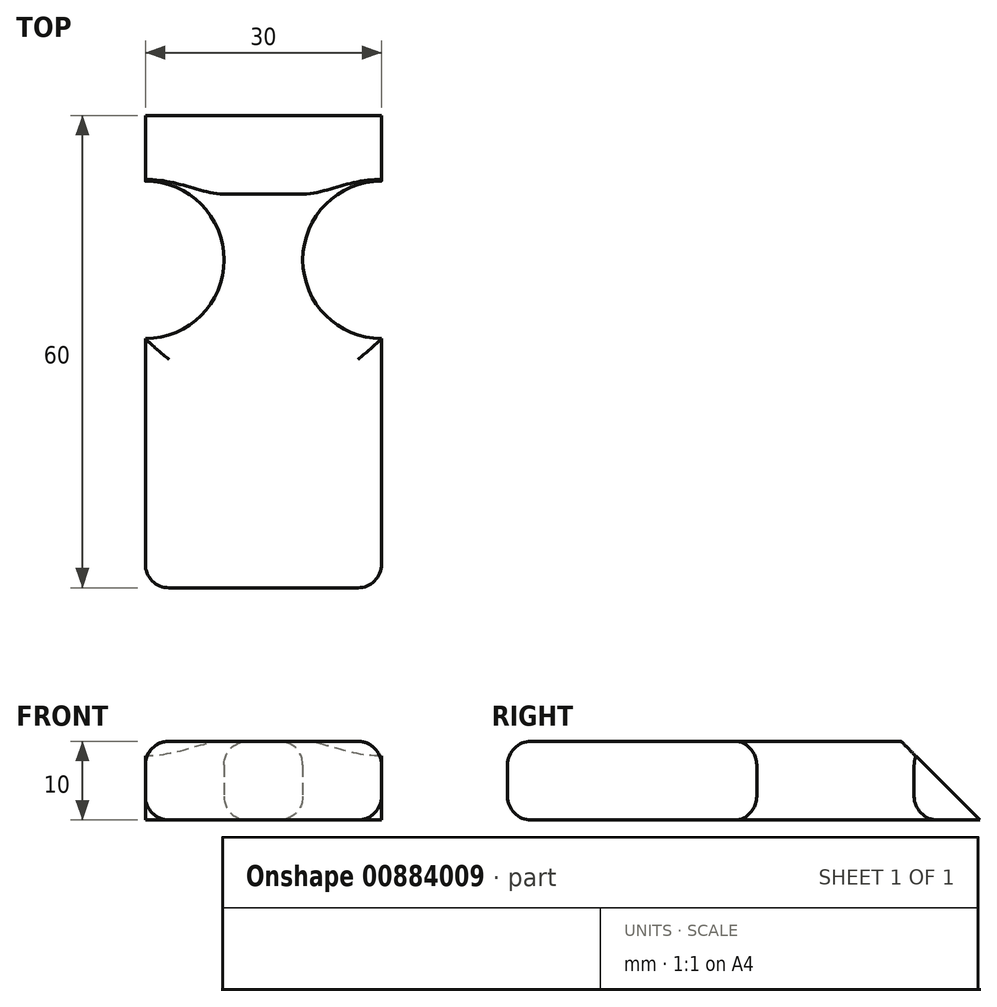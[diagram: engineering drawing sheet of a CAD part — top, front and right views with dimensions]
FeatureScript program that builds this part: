
annotation { "Feature Type Name" : "Feature", "Feature Type Description" : "" }
export const myFeature = defineFeature(function(context is Context, id is Id, definition is map)
    precondition{}
    {
        {
            var Q0;
            Q0=qCreatedBy(makeId("Top.planeOp"),FACE);
            var sketch = newSketch(context, id + "F0", { "sketchPlane" : qUnion([Q0])});
            skLineSegment(sketch, "E0.bottom", {"start": v(-15, 30) * mm, "end": v(15, 30) * mm});
            skLineSegment(sketch, "E0.top", {"start": v(-15, -30) * mm, "end": v(15, -30) * mm});
            skLineSegment(sketch, "E0.left", {"start": v(-15, 30) * mm, "end": v(-15, 21.66) * mm});
            skLineSegment(sketch, "E0.right", {"start": v(15, 30) * mm, "end": v(15, 21.66) * mm});
            skPoint(sketch, "E0.middle", {"position": v(0, 0) * mm});
            skArc(sketch, "E1", {"start": v(-15, 1.66) * mm, "mid": v(-5, 11.66) * mm, "end": v(-15, 21.66) * mm});
            skArc(sketch, "E2", {"start": v(15, 21.66) * mm, "mid": v(5, 11.66) * mm, "end": v(15, 1.66) * mm});
            skLineSegment(sketch, "E3.trimOffspring", {"start": v(15, 1.66) * mm, "end": v(15, -30) * mm});
            skLineSegment(sketch, "E4.trimOffspring", {"start": v(-15, 1.66) * mm, "end": v(-15, -30) * mm});
            skSolve(sketch);
        }
        {
            var Q0;
            Q0=makeQuery(id+"F0.imprint","IMPRINT",FACE,{"disambiguationData":[TD([[makeQuery(id+"F0.imprint","IMPRINT",EDGE,{"derivedFrom":sQuery(id+"F0.wireOp",EDGE,"E0.bottom")}),-1.0]])]});
            extrude(context, id + "F1", {"entities" : qUnion([Q0]), "depth" : 10 * mm, "offsetDistance" : 25 * mm});
        }
        {
            var Q0;
            Q0=makeQuery(id+"F1.opExtrude","CAP_EDGE",EDGE,{"disambiguationData":[OSD([sQuery(id+"F0.wireOp",EDGE,"E1")])],"isStart":false});
            var Q1;
            Q1=makeQuery(id+"F1.opExtrude","CAP_EDGE",EDGE,{"disambiguationData":[OSD([sQuery(id+"F0.wireOp",EDGE,"E2")])],"isStart":false});
            var Q2;
            Q2=makeQuery(id+"F1.opExtrude","CAP_EDGE",EDGE,{"disambiguationData":[OSD([sQuery(id+"F0.wireOp",EDGE,"E2")])],"isStart":true});
            var Q3;
            Q3=makeQuery(id+"F1.opExtrude","CAP_EDGE",EDGE,{"disambiguationData":[OSD([sQuery(id+"F0.wireOp",EDGE,"E1")])],"isStart":true});
            var Q4;
            Q4=makeQuery(id+"F1.opExtrude","CAP_EDGE",EDGE,{"disambiguationData":[OSD([sQuery(id+"F0.wireOp",EDGE,"E0.top")])],"isStart":true});
            var Q5;
            Q5=makeQuery(id+"F1.opExtrude","CAP_EDGE",EDGE,{"disambiguationData":[OSD([sQuery(id+"F0.wireOp",EDGE,"E4.trimOffspring")])],"isStart":true});
            var Q6;
            Q6=makeQuery(id+"F1.opExtrude","CAP_EDGE",EDGE,{"disambiguationData":[OSD([sQuery(id+"F0.wireOp",EDGE,"E3.trimOffspring")])],"isStart":true});
            var Q7;
            Q7=makeQuery(id+"F1.opExtrude","CAP_EDGE",EDGE,{"disambiguationData":[OSD([sQuery(id+"F0.wireOp",EDGE,"E0.top")])],"isStart":false});
            var Q8;
            Q8=makeQuery(id+"F1.opExtrude","CAP_EDGE",EDGE,{"disambiguationData":[OSD([sQuery(id+"F0.wireOp",EDGE,"E3.trimOffspring")])],"isStart":false});
            var Q9;
            Q9=makeQuery(id+"F1.opExtrude","CAP_EDGE",EDGE,{"disambiguationData":[OSD([sQuery(id+"F0.wireOp",EDGE,"E4.trimOffspring")])],"isStart":false});
            var Q10;
            Q10=makeQuery(id+"F1.opExtrude","SWEPT_EDGE",EDGE,{"disambiguationData":[OSD([sQuery(id+"F0.wireOp",EDGE,"E0.top"),sQuery(id+"F0.wireOp",EDGE,"E3.trimOffspring")])]});
            var Q11;
            Q11=makeQuery(id+"F1.opExtrude","SWEPT_EDGE",EDGE,{"disambiguationData":[OSD([sQuery(id+"F0.wireOp",EDGE,"E0.top"),sQuery(id+"F0.wireOp",EDGE,"E4.trimOffspring")])]});
            fillet(context, id + "F2", {"entities" : qUnion([Q0, Q1, Q2, Q3, Q4, Q5, Q6, Q7, Q8, Q9, Q10, Q11]), "radius" : 3 * mm, "tangentPropagation" : true, "allowEdgeOverflow" : false});
        }
        {
            var Q0;
            Q0=makeQuery(id+"F1.opExtrude","CAP_EDGE",EDGE,{"disambiguationData":[OSD([sQuery(id+"F0.wireOp",EDGE,"E0.bottom")])],"isStart":false});
            chamfer(context, id + "F3", {"entities" : qUnion([Q0]), "width" : 10 * mm, "tangentPropagation" : true});
        }
    });
